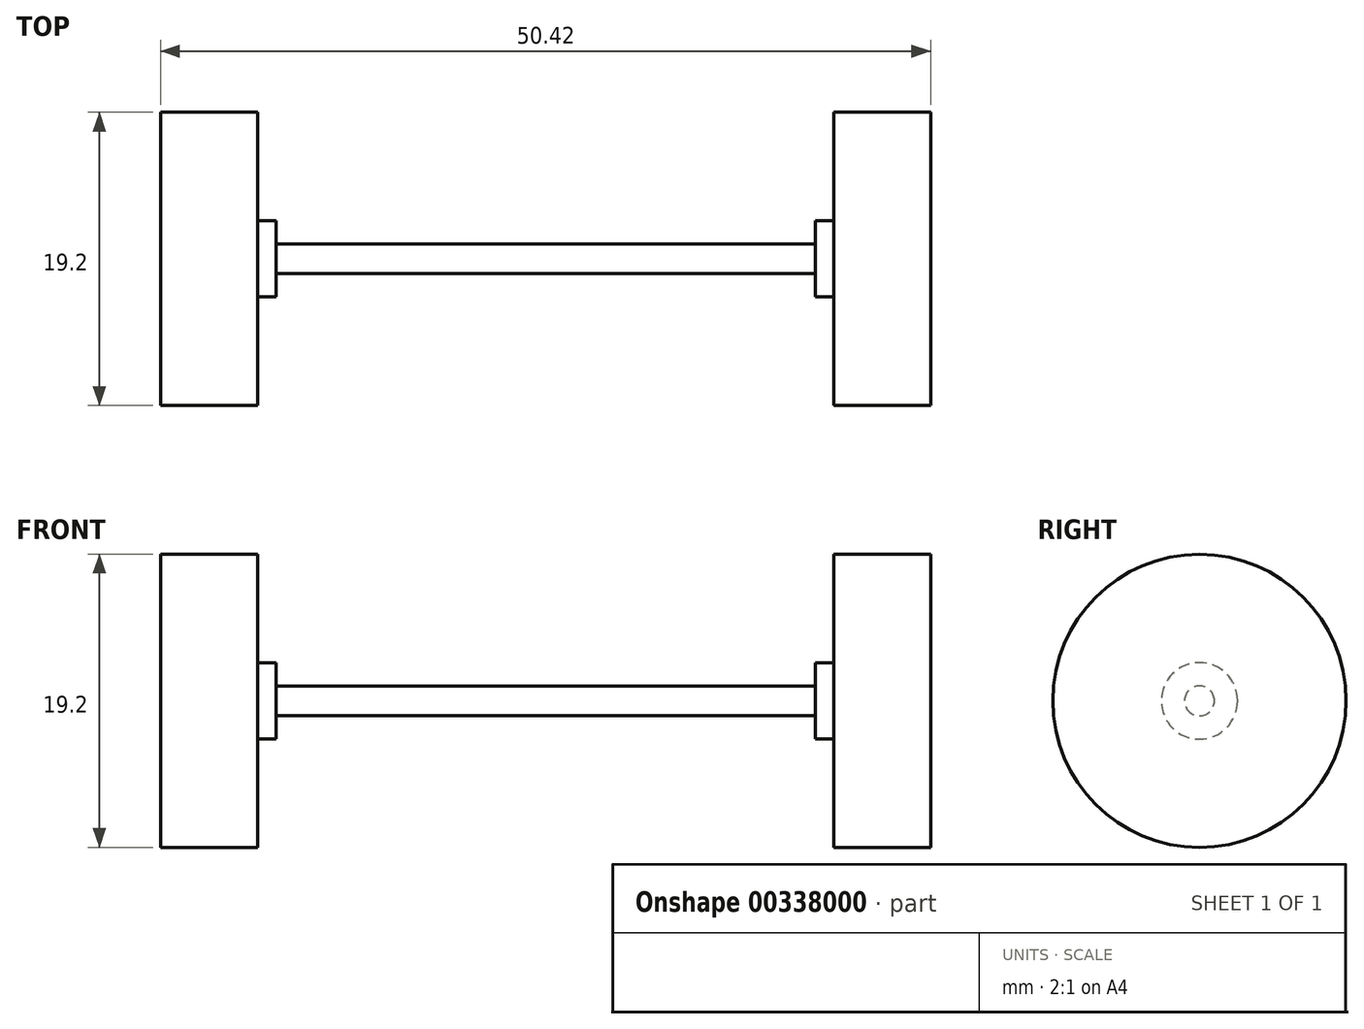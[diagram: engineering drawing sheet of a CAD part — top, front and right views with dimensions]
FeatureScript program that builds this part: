
annotation { "Feature Type Name" : "Feature", "Feature Type Description" : "" }
export const myFeature = defineFeature(function(context is Context, id is Id, definition is map)
    precondition{}
    {
        {
            var Q0;
            Q0=qCreatedBy(makeId("Front.planeOp"),FACE);
            var sketch = newSketch(context, id + "F0", { "sketchPlane" : qUnion([Q0])});
            skLineSegment(sketch, "E0", {"start": v(0, 0) * mm, "end": v(89.7, 0) * mm, "construction": true});
            skLineSegment(sketch, "E1", {"start": v(0, 20.58) * mm, "end": v(0, -19.87) * mm, "construction": true});
            skLineSegment(sketch, "E2", {"start": v(0, 0.98) * mm, "end": v(17.65, 0.98) * mm});
            skLineSegment(sketch, "E3", {"start": v(17.65, 0.98) * mm, "end": v(17.65, 2.5) * mm});
            skLineSegment(sketch, "E4", {"start": v(17.65, 2.5) * mm, "end": v(18.86, 2.5) * mm});
            skLineSegment(sketch, "E5", {"start": v(18.86, 2.5) * mm, "end": v(18.86, 9.6) * mm});
            skLineSegment(sketch, "E6", {"start": v(18.86, 9.6) * mm, "end": v(25.2, 9.6) * mm});
            skLineSegment(sketch, "E7", {"start": v(25.2, 9.6) * mm, "end": v(25.2, 0) * mm});
            skLineSegment(sketch, "E8.MirrorCS", {"start": v(-17.65, 0.98) * mm, "end": v(-17.65, 2.5) * mm});
            skLineSegment(sketch, "E9.MirrorCS", {"start": v(-17.65, 2.5) * mm, "end": v(-18.86, 2.5) * mm});
            skLineSegment(sketch, "E10.MirrorCS", {"start": v(0, 0.98) * mm, "end": v(-17.65, 0.98) * mm});
            skLineSegment(sketch, "E11.MirrorCS", {"start": v(-18.86, 2.5) * mm, "end": v(-18.86, 9.6) * mm});
            skLineSegment(sketch, "E12.MirrorCS", {"start": v(-25.2, 9.6) * mm, "end": v(-25.2, 0) * mm});
            skLineSegment(sketch, "E13.MirrorCS", {"start": v(-18.86, 9.6) * mm, "end": v(-25.2, 9.6) * mm});
            skLineSegment(sketch, "E14", {"start": v(-25.2, 0) * mm, "end": v(25.2, 0) * mm});
            skSolve(sketch);
        }
        {
            var Q0;
            Q0 = qSketchRegion(id + "F0", true);
            var Q1;
            Q1=sQuery(id+"F0.wireOp",EDGE,"E0");
            revolve(context, id + "F1", {"entities" : qUnion([Q0]), "axis" : qUnion([Q1]), "revolveType" : RevolveType.FULL});
        }
    });
